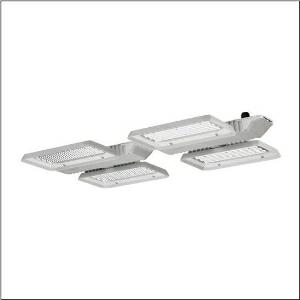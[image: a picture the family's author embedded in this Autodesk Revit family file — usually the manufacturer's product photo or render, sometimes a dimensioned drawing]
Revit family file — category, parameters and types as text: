
# Revit family: highbay_11_51hla1d24mca
name_source: partatom
category: Lighting Fixtures
units: mm (PartAtom-declared; Revit-internal decimal feet)

## family parameters
Cut with Voids When Loaded = No
Host = Face
Light Source = No
Part Type = Normal
Room Calculation Point = No
Round Connector Dimension = Use Diameter
Shared = No

## types (1)
- --- (1 x LED, 28120 lm, 162.4 W, 4000K)
    Apparent Load = 162 VA
    CIE Flux Codes = 88 95 99 100 99
    Color Rendering = 80
    Color Temperature = 4000K
    Default Elevation = 1800 mm
    Description = Highbay 11, LED high bay luminaire, primary light control with lens, of PMMA, light emission: direct distribution, primary light characteristic: symmetric, installation type: suspended mounting, surface-mounted, for 2x 2 x LED rated luminous flux: 28.120 lm, light colour: 840, colour temperature: 4000K, control gear: ECG DALI, with terminal, 5-pole, max. 2.5mm², mains connection: 230..240V, AC, 50/60Hz, rated input power: 162W, LED unit, of diecast aluminium, unplated, bead blasted, silver, length: 940 mm, width: 500 mm, height: 65mm, housing, of diecast aluminium, uncoated, bead blasted, silver, protection rating (complete): IP65, insulation class (complete): insulation class I (protective earthing), certification: CE, ENEC, VDE, protection symbol: D, impact resistance: IK08 with glass or PC cover, permissible ambient temperature for indoor applications: -35..+55°C, reducing of maximum allowable ambient temperature of 5°C with ceiling mounting, corresponds to IFS (International Featured Standards) requirements for safety and quality in the food industry, packaging unit: 1 piece
    Height = 95 mm
    Lamp = 1 x LED
    Lamp Light Flux = 28120 lm
    Lamp Power = 162.4 W
    Lamp count = 1
    Length = 939 mm
    Luminous efficacy = 173 lm/W
    Manufacturer = Siteco
    ModVariant = No
    Model = 51HLA1D24MCA
    Mounting Place = Ceiling
    Mounting Type = Pendant
    Number of Poles = 1
    OnlyDefault = Yes
    Power Factor = 1
    Product Name = Highbay 11
    Product group = LED high bay luminaire
    ProductGroupID = 903
    Protection Class = Protection class I
    Protection Degree = IP 65
    RLX_Detail_Level = 1
    RlxData = <blob elided: 100089 chars, md5=73557c4f>
    Socket = socket
    Standby Power = 0 W
    System Light Flux = 28120 lm
    System Power = 162 W
    Type Comments = factory setting: luminous flux: 100 % | dim-lin: 254 | 460 mA
    Type Image = l_1003428.jpg
    URL = http://relux.com
    VarID = @adj_141125
    Voltage = 0 V
    Weight = 0.00 kg
    Width = 501 mm

## geometry (parser evidence)
native form markers: Blend x4, Sweep x12
no freeform markers — native parametric forms only
